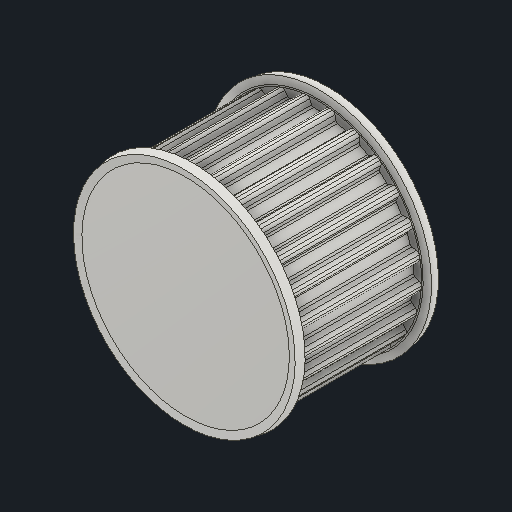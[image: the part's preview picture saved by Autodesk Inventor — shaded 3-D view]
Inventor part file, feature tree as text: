
AUTODESK INVENTOR PART (.ipt)
format: ipt  version: 2023.1 (Build 271208000, 208)  size: 424,448 bytes
history: native  units: mm (DEFAULTED — no unit token found)
features: other x3, extrude x2, fillet x1, pattern_circular x1
ambient origin geometry x8: Origin, YZ Plane, XZ Plane, XY Plane, X Axis, Y Axis, Z Axis, Center Point
bodies: Solid1 (feature_tree)
feature tree (7):
  other  "Pulley Sketch"
  extrude  "Base Body"  Depth=19.894368mm
  extrude  "Tooth"  Depth=0.3mm
  fillet  "Tooth Fillet"  Radius=0.75mm
  pattern_circular  "Teeth"  [2 undecoded]
  other  "Left flange"
  other  "Right flange"
note: 2 required parameter values undecoded (feature->parameter linkage not recoverable at this tier; creation-order binding heuristic only, values carry confidence <= 0.55)
